# Revit family: UN552V
name_source: partatom
category: Generic Models
revit_build: Autodesk Revit Architecture 2014 (Build: 20130308_1515(x64)
units: mm (PartAtom-declared; Revit-internal decimal feet)

## types (1)
- UN552V
    CONNECTIVITY- Input Terminals- Analog = VGA 15-pin D-sub, RCA Composite
    CONNECTIVITY- Input Terminals- Audio = Audio Mini Jack x2, DisplayPort Audio, HDMI Audio
    CONNECTIVITY- Input Terminals- Data = microSD (Media Player), USB 2.0 (Media Player), USB 2.0 (Service), USB Type-B (Upstream), USB 2.0 x2 (Compute Module, USB CM1 is Powered 5V/2A)
    CONNECTIVITY- Input Terminals- Digital = HDMI x2 (1.4/2.0), DisplayPort x2 (1.1/1.2), DVI-D
    CONNECTIVITY- Input Terminals- External Control = RS232C, LAN (100Mb), 3.5 Mini Jack (IR Remote)
    CONNECTIVITY- Output Terminals- Audio = 3.5mm Mini-Jack, External Speaker Jack x2
    CONNECTIVITY- Output Terminals- Digital = DisplayPort (Outputs DisplayPort1 and OPTION (DP)), HDMI (Outputs HDMI1, DVI and OPTION (TMDS))
    CONNECTIVITY- Output Terminals- External Control = LAN (100Mb)
    Description = NEC LCD Video Wall Display
    ENVIRONMENTAL CONDITIONS- Operating Altitude = 9843 ft. / 3000m
    ENVIRONMENTAL CONDITIONS- Operating Humidity = 0 - 90%
    ENVIRONMENTAL CONDITIONS- Operating Temperature = 0 - 50°C / 32 - 122°F
    LCD MODULE- Aspect Ratio = 16 : 9
    LCD MODULE- Brightness (Typical/Minimum) = 350 cd/sqm / 500 cd/sqm
    LCD MODULE- Contrast Ratio (Typical) = 1100:1 (without local dimming)
    LCD MODULE- Displayable Colors = Over 1.07 Billion
    LCD MODULE- Native Resolution = 1920 x 1080
    LCD MODULE- Orientation = Landscape / Portrait
    LCD MODULE- Panel Haze (%) = 28
    LCD MODULE- Panel Technology = S-IPS
    LCD MODULE- Viewable Image Size = 55"
    LCD MODULE- Viewing Angle = 178 / 178
    Manufacturer = NEC Display Solutions
    Model = UN552V
    PHYSICAL SPECS- Bezel Width (L/R, T/B) = 2.3mm/1.2mm, 1.2mm/2.3mm
    PHYSICAL SPECS- Net Dimensions (w/o Stand, WxHxD) = 47.8 x 26.9 x 4.1 in. / 1213.4 x 684.2 x 103.8mm
    PHYSICAL SPECS- Net Weight (w/o Stand) = 61.9 lbs. / 28.1 kg
    PHYSICAL SPECS- Vesa Hole Configuration = 400 x 400 (4-hole, M6)
    POWER CONSUMPTION- Current Rating = 3.6A @ 100V, 1.4A @ 240V
    POWER CONSUMPTION- Network Standby = 2W
    POWER CONSUMPTION- Power Consumption (Typical/Max Brightness/ Absolute Max) = 110W/165W/315W
    POWER CONSUMPTION- Speaker Rating = Integrated 10W x 10W, Optional 15W x 2
    POWER CONSUMPTION- Standby = 0.5W
    URL = www.necdisplay.com

## geometry (parser evidence)
native form markers: Sweep x2
no freeform markers — native parametric forms only
